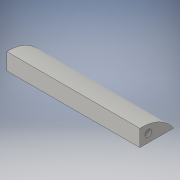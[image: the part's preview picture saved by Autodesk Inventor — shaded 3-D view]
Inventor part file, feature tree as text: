
AUTODESK INVENTOR PART (.ipt)
format: ipt  version: 2016 (Build 200138000, 138)  size: 96,768 bytes
history: native  units: in
note: dims shown in document units (in); Inventor stores cm internally (conversion verified against a paired STEP export)
features: extrude x1, hole x1, sketch x1
ambient origin geometry x8: Origin, YZ Plane, XZ Plane, XY Plane, X Axis, Y Axis, Z Axis, Center Point
bodies: Body1 (feature_tree)
feature tree (3):
  extrude  "Extrusion2"  Depth=1.0in
  hole  "Hole2"  [1 undecoded]
  sketch  "Sketch1"  dims[d14=0.25in d15=0.125in d16=1.0in d17=0.0in d18=0.063in d19=0.063in d20=0.05in d21=0.75in d22=0.375in d23=0.25in d24=0.5635in d25=1.0in d26=0.8108in]
note: 1 required parameter value undecoded (feature->parameter linkage not recoverable at this tier; creation-order binding heuristic only, values carry confidence <= 0.55)
